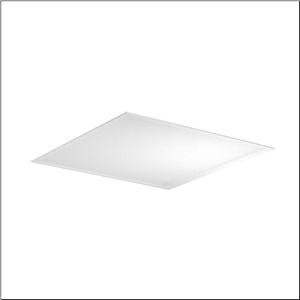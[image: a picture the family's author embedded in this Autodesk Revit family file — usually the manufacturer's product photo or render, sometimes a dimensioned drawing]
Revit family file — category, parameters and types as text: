
# Revit family: apollon_r__21_square_51mq12wd2m14_c270
name_source: partatom
category: Lighting Fixtures
units: mm (PartAtom-declared; Revit-internal decimal feet)

## family parameters
Cut with Voids When Loaded = No
Host = Face
Light Source = No
Part Type = Normal
Room Calculation Point = No
Round Connector Dimension = Use Diameter
Shared = No

## types (1)
- --- (1 x LED, 4200 lm, 26 W, 4000K)
    Apparent Load = 26 VA
    CIE Flux Codes = 60 87 97 100 100
    Color Rendering = 80
    Color Temperature = 4000K
    Default Elevation = 1800 mm
    Description = Apollon® 21 square, office luminaire, primary optical cover: micro prismatic cover, of PMMA, CAT 2 (L<= 3000cd/m²), light emission: direct distribution, primary light characteristic: symmetric, installation type: lay-in mounting, LED, rated luminous flux: 4.200lm, luminous efficacy: 162lm/W, light colour: 830/840, colour temperature: 3000/4000K, with terminal, 5-pole, mains connection: 220..240V, AC/DC, 0/50..60Hz, rated input power: 26W, housing, of aluminium, coated, traffic white (RAL 9016), module: M600, length: 595mm, width: 595mm, height: 30mm, housing upper side, of sheet steel, galvanised, protection rating (complete): IP20, protection rating (lamp compartment, on room side): IP50, insulation class (complete): insulation class II (safety insulation), certification: CE, ENEC, impact resistance: IK03, permissible operating ambient temperature: -20..+45°C, permissible storage temperature: -40..+80°C, packaging unit: 1 piece
    Height = 0 mm  [stored 0 ft]
    Lamp = 1 x LED
    Lamp Light Flux = 4200 lm
    Lamp Power = 26 W
    Lamp count = 1
    Length = 595 mm
    Luminous efficacy = 162 lm/W
    Manufacturer = Siteco
    ModVariant = No
    Model = 51MQ12WD2M14
    Mounting Place = Ceiling
    Mounting Type = Recessed
    Number of Poles = 1
    OnlyDefault = Yes
    Power Factor = 1
    Product Name = Apollon® 21 square
    Product group = office luminaire | ceiling recessed
    ProductGroupID = 401
    Protection Class = Protection class II
    Protection Degree = IP 20
    RLX_Detail_Level = 1
    RLX_Emergency_Light_Flux = 0 lm
    RLX_Emergency_Type = 0
    RLX_Emergency_Type_DB = No
    RlxData = <blob elided: 12681 chars, md5=cb1ee323>
    Socket = socket
    Standby Power = 0 W
    System Light Flux = 4200 lm
    System Power = 26 W
    Type Comments = factory setting
    Type Image = l_1291049.jpg
    URL = http://relux.com
    VarID = @adj_026981
    Voltage = 0 V
    Weight = 0.00 kg
    Width = 595 mm

note: [stored X ft] marks values corroborated as IEEE doubles in the binary element streams (Revit-internal decimal feet)

## geometry (parser evidence)
native form markers: Sweep x9
no freeform markers — native parametric forms only
